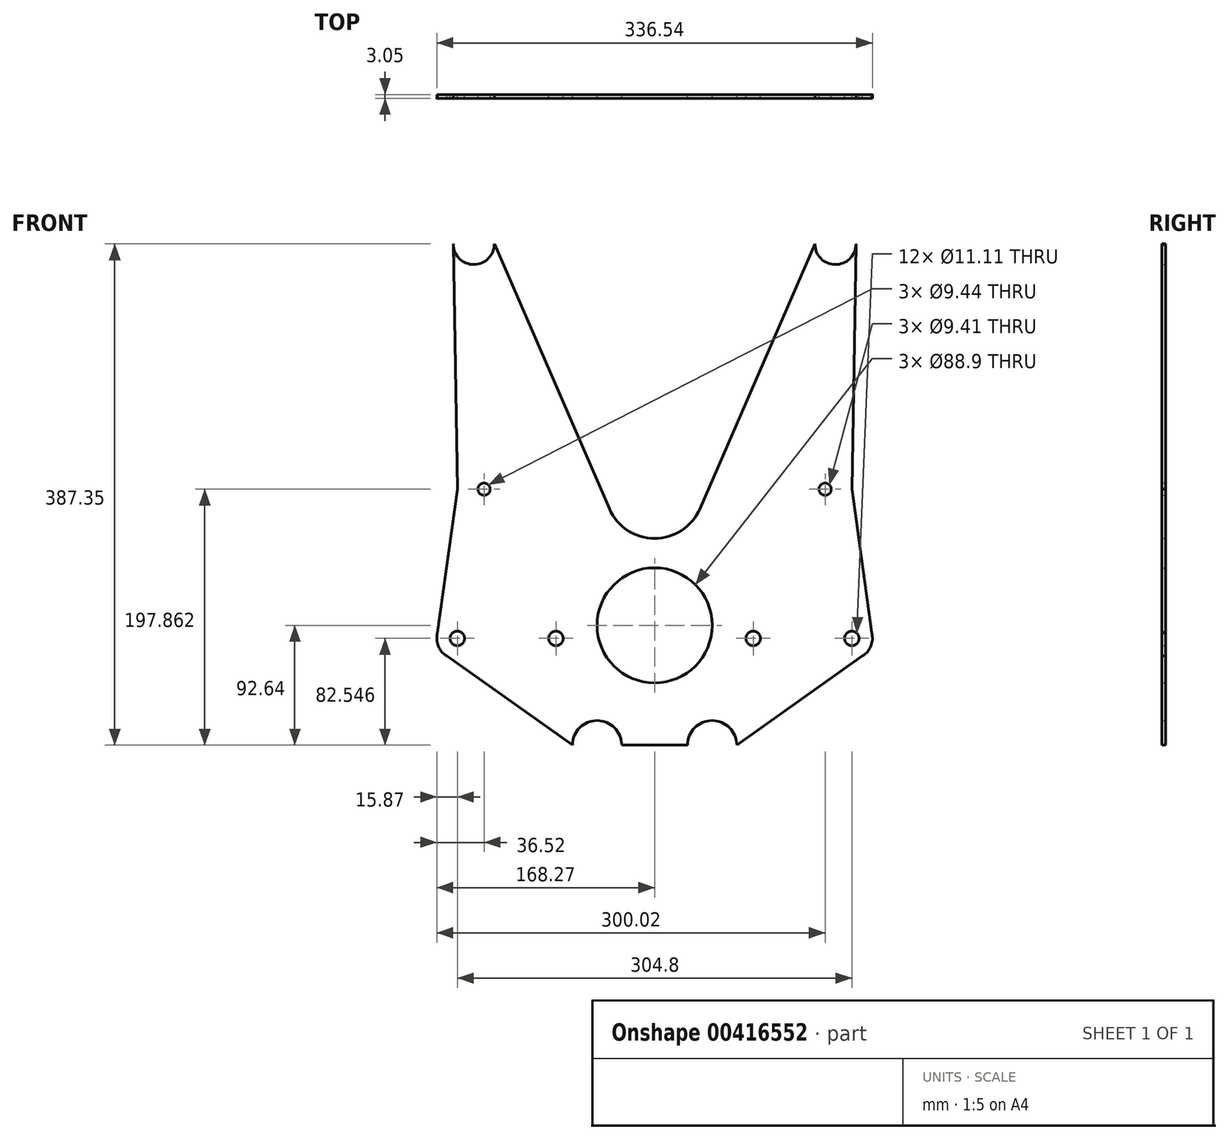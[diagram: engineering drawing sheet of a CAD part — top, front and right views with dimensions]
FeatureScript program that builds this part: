
annotation { "Feature Type Name" : "Feature", "Feature Type Description" : "" }
export const myFeature = defineFeature(function(context is Context, id is Id, definition is map)
    precondition{}
    {
        {
            var Q0;
            Q0=qCreatedBy(makeId("Front.planeOp"),FACE);
            var sketch = newSketch(context, id + "F0", { "sketchPlane" : qUnion([Q0])});
            skLineSegment(sketch, "E0.bottom", {"start": v(20.57, -20.57) * mm, "end": v(-20.57, -20.57) * mm, "construction": true});
            skLineSegment(sketch, "E0.top", {"start": v(20.57, 20.57) * mm, "end": v(-20.57, 20.57) * mm, "construction": true});
            skLineSegment(sketch, "E0.left", {"start": v(20.57, -20.57) * mm, "end": v(20.57, 20.57) * mm, "construction": true});
            skLineSegment(sketch, "E0.right", {"start": v(-20.57, -20.57) * mm, "end": v(-20.57, 20.57) * mm, "construction": true});
            skPoint(sketch, "E0.middle", {"position": v(0, 0) * mm});
            skPoint(sketch, "E1", {"position": v(20.57, -15.81) * mm});
            skPoint(sketch, "E2", {"position": v(-20.57, -15.81) * mm});
            skLineSegment(sketch, "E3", {"start": v(0, -15.81) * mm, "end": v(152.4, -15.81) * mm, "construction": true});
            skPoint(sketch, "E3.startSnap0", {"position": v(0, -20.57) * mm});
            skLineSegment(sketch, "E4", {"start": v(0, -15.81) * mm, "end": v(-152.4, -15.81) * mm, "construction": true});
            skCircle(sketch, "E5", {"center": v(-152.4, -10.1) * mm, "radius": 5.56 * mm});
            skCircle(sketch, "E6", {"center": v(152.4, -10.1) * mm, "radius": 5.56 * mm});
            skCircle(sketch, "E7", {"center": v(76.2, -10.1) * mm, "radius": 5.56 * mm});
            skCircle(sketch, "E8", {"center": v(-76.2, -10.1) * mm, "radius": 5.56 * mm});
            skPoint(sketch, "E9", {"position": v(-152.4, 105.22) * mm});
            skLineSegment(sketch, "E10", {"start": v(0, 0) * mm, "end": v(0, 140.85) * mm, "construction": true});
            skPoint(sketch, "E10.endSnap0", {"position": v(0, 20.57) * mm});
            skLineSegment(sketch, "E11", {"start": v(-152.4, -10.1) * mm, "end": v(-152.4, -92.64) * mm, "construction": true});
            skLineSegment(sketch, "E12", {"start": v(-152.4, -10.1) * mm, "end": v(-152.4, 294.7) * mm, "construction": true});
            skLineSegment(sketch, "E13", {"start": v(-152.4, 105.22) * mm, "end": v(152.4, 105.22) * mm, "construction": true});
            skCircle(sketch, "E14", {"center": v(-131.75, 105.22) * mm, "radius": 4.72 * mm});
            skCircle(sketch, "E15", {"center": v(131.75, 105.22) * mm, "radius": 4.7 * mm});
            skLineSegment(sketch, "E16", {"start": v(-152.4, -92.64) * mm, "end": v(152.4, -92.64) * mm, "construction": true});
            skPoint(sketch, "E17", {"position": v(-44.45, -92.64) * mm});
            skLineSegment(sketch, "E18", {"start": v(0, -20.57) * mm, "end": v(0, -115.22) * mm, "construction": true});
            skPoint(sketch, "E19", {"position": v(44.45, -92.64) * mm});
            skArc(sketch, "E20", {"start": v(-25.4, -92.64) * mm, "mid": v(-44.45, -73.6) * mm, "end": v(-63.5, -92.64) * mm});
            skArc(sketch, "E21", {"start": v(63.5, -92.64) * mm, "mid": v(44.45, -73.6) * mm, "end": v(25.4, -92.64) * mm});
            skLineSegment(sketch, "E22", {"start": v(-25.4, -92.64) * mm, "end": v(25.4, -92.64) * mm});
            skLineSegment(sketch, "E23", {"start": v(0, 0) * mm, "end": v(0, 293.77) * mm, "construction": true});
            skLineSegment(sketch, "E24", {"start": v(152.4, 294.7) * mm, "end": v(-152.4, 294.7) * mm, "construction": true});
            skPoint(sketch, "E25", {"position": v(-139.7, 294.7) * mm});
            skPoint(sketch, "E26", {"position": v(139.7, 294.7) * mm});
            skArc(sketch, "E27", {"start": v(-155.58, 294.7) * mm, "mid": v(-155.57, 294.44) * mm, "end": v(-155.57, 294.17) * mm});
            skArc(sketch, "E28", {"start": v(155.57, 294.17) * mm, "mid": v(155.57, 294.44) * mm, "end": v(155.58, 294.7) * mm});
            skArc(sketch, "E29", {"start": v(160.54, -23.72) * mm, "mid": v(167.15, -15.97) * mm, "end": v(167.68, -5.8) * mm});
            skArc(sketch, "E30", {"start": v(-167.68, -5.8) * mm, "mid": v(-167.15, -15.97) * mm, "end": v(-160.54, -23.72) * mm});
            skLineSegment(sketch, "E31", {"start": v(155.58, 294.7) * mm, "end": v(155.57, 294.17) * mm});
            skLineSegment(sketch, "E32", {"start": v(152.4, 105.22) * mm, "end": v(168.28, -10.1) * mm});
            skLineSegment(sketch, "E33", {"start": v(-155.58, 294.7) * mm, "end": v(-152.4, 105.22) * mm});
            skLineSegment(sketch, "E34", {"start": v(-152.4, 105.22) * mm, "end": v(-168.28, -10.1) * mm});
            skLineSegment(sketch, "E35", {"start": v(155.58, 294.7) * mm, "end": v(152.4, 105.22) * mm});
            skLineSegment(sketch, "E36", {"start": v(162.59, -22.27) * mm, "end": v(63.5, -92.64) * mm});
            skLineSegment(sketch, "E37", {"start": v(-162.59, -22.27) * mm, "end": v(-63.5, -92.64) * mm});
            skPoint(sketch, "E38.orphan", {"position": v(-25.4, 196.65) * mm});
            skPoint(sketch, "E39.center.orphan", {"position": v(0, 196.65) * mm});
            skPoint(sketch, "E40.end.orphan", {"position": v(25.4, 196.65) * mm});
            skArc(sketch, "E41", {"start": v(-34.95, 90.05) * mm, "mid": v(0, 67.12) * mm, "end": v(34.95, 90.05) * mm});
            skLineSegment(sketch, "E42", {"start": v(-123.83, 294.7) * mm, "end": v(-34.95, 90.05) * mm});
            skLineSegment(sketch, "E43", {"start": v(123.83, 294.7) * mm, "end": v(34.95, 90.05) * mm});
            skArc(sketch, "E44", {"start": v(-155.58, 294.7) * mm, "mid": v(-139.7, 278.83) * mm, "end": v(-123.83, 294.7) * mm});
            skArc(sketch, "E45", {"start": v(123.83, 294.7) * mm, "mid": v(139.7, 278.83) * mm, "end": v(155.58, 294.7) * mm});
            skCircle(sketch, "E46", {"center": v(0, 0) * mm, "radius": 44.45 * mm});
            skSolve(sketch);
        }
        {
            var Q0;
            Q0=qSketchRegion(id+"F0",true);
            extrude(context, id + "F1", {"entities" : qUnion([Q0]), "depth" : 3.05 * mm});
        }
        {
            var Q0;
            Q0=qSketchRegion(id+"F0",true);
            extrude(context, id + "F2", {"entities" : qUnion([Q0]), "depth" : 3.05 * mm});
        }
        {
            var Q0;
            Q0 = qSketchRegion(id + "F0", true);
            extrude(context, id + "F3", {"entities" : qUnion([Q0]), "depth" : 3.05 * mm});
        }
    });
